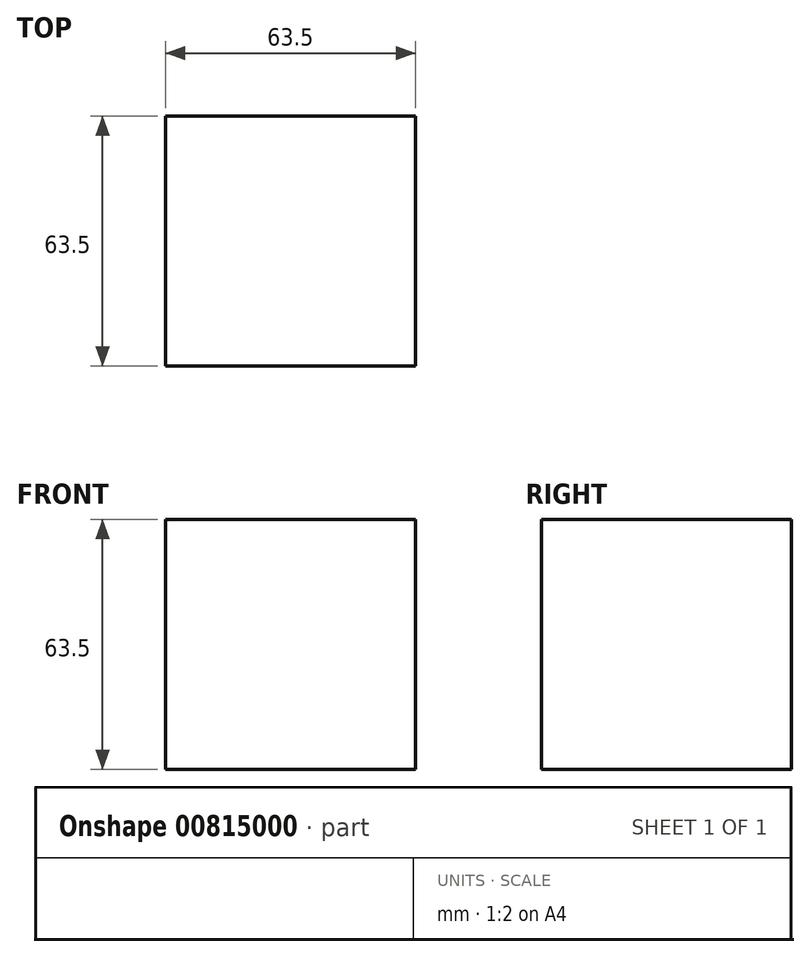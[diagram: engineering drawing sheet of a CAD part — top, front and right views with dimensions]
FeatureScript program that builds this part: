
annotation { "Feature Type Name" : "Feature", "Feature Type Description" : "" }
export const myFeature = defineFeature(function(context is Context, id is Id, definition is map)
    precondition{}
    {
        {
            var Q0;
            Q0=qCreatedBy(makeId("Front.planeOp"),FACE);
            var sketch = newSketch(context, id + "F0", { "sketchPlane" : qUnion([Q0])});
            skLineSegment(sketch, "E0.bottom", {"start": v(31.75, 31.75) * mm, "end": v(-31.75, 31.75) * mm});
            skLineSegment(sketch, "E0.top", {"start": v(31.75, -31.75) * mm, "end": v(-31.75, -31.75) * mm});
            skLineSegment(sketch, "E0.left", {"start": v(31.75, 31.75) * mm, "end": v(31.75, -31.75) * mm});
            skLineSegment(sketch, "E0.right", {"start": v(-31.75, 31.75) * mm, "end": v(-31.75, -31.75) * mm});
            skPoint(sketch, "E0.middle", {"position": v(0, 0) * mm});
            skSolve(sketch);
        }
        {
            var Q0;
            Q0 = qSketchRegion(id + "F0", true);
            extrude(context, id + "F1", {"entities" : qUnion([Q0]), "endBound" : BoundingType.SYMMETRIC, "depth" : 63.5 * mm, "offsetDistance" : 25.4 * mm});
        }
    });
